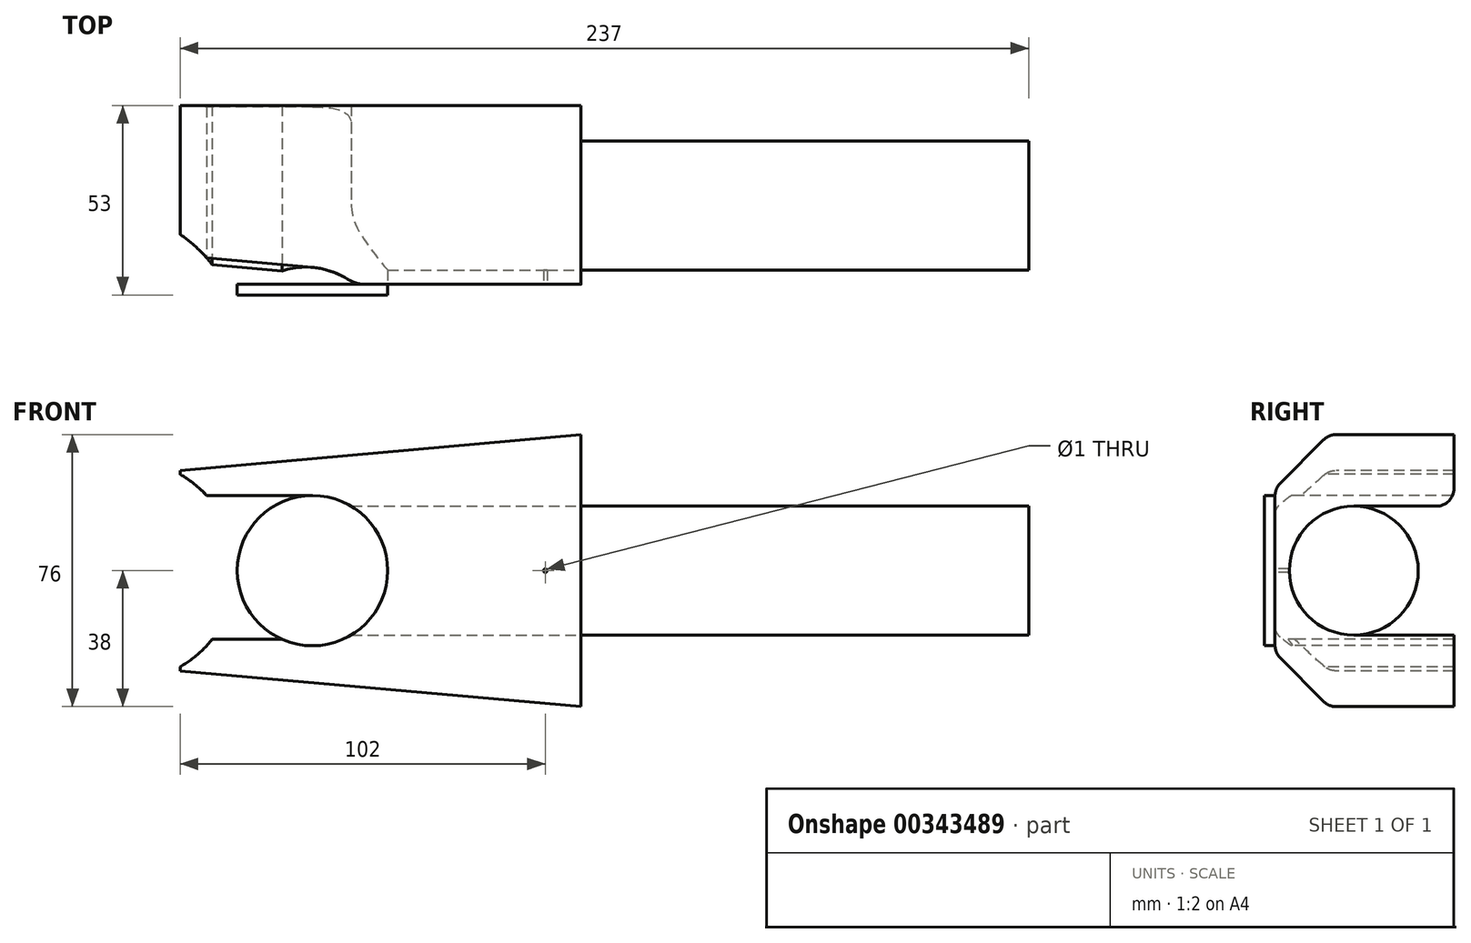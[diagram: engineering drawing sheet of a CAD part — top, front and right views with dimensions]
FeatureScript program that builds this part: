
annotation { "Feature Type Name" : "Feature", "Feature Type Description" : "" }
export const myFeature = defineFeature(function(context is Context, id is Id, definition is map)
    precondition{}
    {
        {
            var Q0;
            Q0=qCreatedBy(makeId("Front.planeOp"),FACE);
            var sketch = newSketch(context, id + "F0", { "sketchPlane" : qUnion([Q0])});
            skCircle(sketch, "E0", {"center": v(0, 0) * mm, "radius": 21 * mm});
            skLineSegment(sketch, "E1", {"start": v(-83.93, 0) * mm, "end": v(59.81, 0) * mm});
            skCircle(sketch, "E2", {"center": v(-52.37, 0) * mm, "radius": 30 * mm});
            skSolve(sketch);
        }
        {
            var Q0;
            Q0=qSketchRegion(id+"F0",true);
            extrude(context, id + "F1", {"entities" : qUnion([Q0]), "endBound" : BoundingType.SYMMETRIC, "depth" : 50 * mm});
        }
        {
            var Q0;
            Q0=qCreatedBy(makeId("Right.planeOp"),FACE);
            var sketch = newSketch(context, id + "F2", { "sketchPlane" : qUnion([Q0])});
            skCircle(sketch, "E3", {"center": v(0, 0) * mm, "radius": 18 * mm});
            skSolve(sketch);
        }
        {
            var Q0;
            Q0=qSketchRegion(id+"F2",true);
            extrude(context, id + "F3", {"entities" : qUnion([Q0]), "operationType" : NewBodyOperationType.ADD, "depth" : 200 * mm});
        }
        {
            var Q0;
            Q0=qCreatedBy(makeId("Front.planeOp"),FACE);
            cPlane(context, id + "F4", {"entities" : qUnion([Q0]), "cplaneType" : CPlaneType.OFFSET, "offset" : 18 * mm, "width" : 150 * mm, "height" : 150 * mm});
        }
        {
            var Q0;
            Q0=qCreatedBy(id+"F4.planeOp",FACE);
            var sketch = newSketch(context, id + "F5", { "sketchPlane" : qUnion([Q0])});
            skCircle(sketch, "E4", {"center": v(65, 0) * mm, "radius": 2.5 * mm});
            skSolve(sketch);
        }
        {
            var Q0;
            Q0=qSketchRegion(id+"F5",true);
            extrude(context, id + "F6", {"entities" : qUnion([Q0]), "operationType" : NewBodyOperationType.REMOVE, "oppositeDirection" : true, "depth" : 30 * mm});
        }
        {
            var Q0;
            Q0=qCreatedBy(makeId("Right.planeOp"),FACE);
            cPlane(context, id + "F7", {"entities" : qUnion([Q0]), "cplaneType" : CPlaneType.OFFSET, "offset" : 10 * mm, "oppositeDirection" : true, "width" : 150 * mm, "height" : 150 * mm});
        }
        {
            var Q0;
            Q0=qCreatedBy(id+"F7.planeOp",FACE);
            var sketch = newSketch(context, id + "F8", { "sketchPlane" : qUnion([Q0])});
            skLineSegment(sketch, "E5", {"start": v(0, 48.61) * mm, "end": v(0, -58.43) * mm});
            skLineSegment(sketch, "E6", {"start": v(-60.37, 0) * mm, "end": v(50.93, 0) * mm});
            skLineSegment(sketch, "E7", {"start": v(0, 24) * mm, "end": v(-10, 24) * mm});
            skLineSegment(sketch, "E8", {"start": v(-10, 24) * mm, "end": v(-10, 28) * mm});
            skLineSegment(sketch, "E9", {"start": v(-10, 28) * mm, "end": v(-1, 28) * mm});
            skLineSegment(sketch, "E10", {"start": v(-1, 28) * mm, "end": v(-1, 29) * mm});
            skLineSegment(sketch, "E11", {"start": v(-1, 29) * mm, "end": v(0, 29) * mm});
            skLineSegment(sketch, "E12.MirrorCS", {"start": v(10, 28) * mm, "end": v(1, 28) * mm});
            skLineSegment(sketch, "E13.MirrorCS", {"start": v(10, 24) * mm, "end": v(10, 28) * mm});
            skLineSegment(sketch, "E14.MirrorCS", {"start": v(0, 24) * mm, "end": v(10, 24) * mm});
            skLineSegment(sketch, "E15.MirrorCS", {"start": v(1, 29) * mm, "end": v(0, 29) * mm});
            skLineSegment(sketch, "E16.MirrorCS", {"start": v(1, 28) * mm, "end": v(1, 29) * mm});
            skLineSegment(sketch, "E17.MirrorCS", {"start": v(1, -28) * mm, "end": v(1, -29) * mm});
            skLineSegment(sketch, "E18.MirrorCS", {"start": v(1, -29) * mm, "end": v(0, -29) * mm});
            skLineSegment(sketch, "E19.MirrorCS", {"start": v(-1, -28) * mm, "end": v(-1, -29) * mm});
            skLineSegment(sketch, "E20.MirrorCS", {"start": v(-1, -29) * mm, "end": v(0, -29) * mm});
            skLineSegment(sketch, "E21.MirrorCS", {"start": v(10, -24) * mm, "end": v(10, -28) * mm});
            skLineSegment(sketch, "E22.MirrorCS", {"start": v(0, -24) * mm, "end": v(10, -24) * mm});
            skLineSegment(sketch, "E23.MirrorCS", {"start": v(0, -24) * mm, "end": v(-10, -24) * mm});
            skLineSegment(sketch, "E24.MirrorCS", {"start": v(-10, -24) * mm, "end": v(-10, -28) * mm});
            skLineSegment(sketch, "E25.MirrorCS", {"start": v(-10, -28) * mm, "end": v(-1, -28) * mm});
            skLineSegment(sketch, "E26.MirrorCS", {"start": v(10, -28) * mm, "end": v(1, -28) * mm});
            skSolve(sketch);
        }
        {
            var Q0;
            {var subQ0=sQuery(id+"F8.wireOp",EDGE,"E7");Q0=makeQuery(id+"F8.imprint","IMPRINT",FACE,{"disambiguationData":[TD([[makeQuery(id+"F8.imprint","IMPRINT",EDGE,{"derivedFrom":subQ0}),-1.0]])]});}
            var Q1;
            Q1=makeQuery(id+"F8.imprint","IMPRINT",FACE,{"disambiguationData":[TD([[makeQuery(id+"F8.imprint","IMPRINT",EDGE,{"derivedFrom":sQuery(id+"F8.wireOp",EDGE,"E12.MirrorCS")}),1.0]])]});
            var Q2;
            Q2=makeQuery(id+"F8.imprint","IMPRINT",FACE,{"disambiguationData":[TD([[makeQuery(id+"F8.imprint","IMPRINT",EDGE,{"derivedFrom":sQuery(id+"F8.wireOp",EDGE,"E19.MirrorCS")}),1.0]])]});
            var Q3;
            Q3=makeQuery(id+"F8.imprint","IMPRINT",FACE,{"disambiguationData":[TD([[makeQuery(id+"F8.imprint","IMPRINT",EDGE,{"derivedFrom":sQuery(id+"F8.wireOp",EDGE,"E17.MirrorCS")}),-1.0]])]});
            extrude(context, id + "F9", {"entities" : qUnion([Q0, Q1, Q2, Q3]), "depth" : 85 * mm});
        }
        {
            var Q0;
            Q0=makeQuery(id+"F9.opExtrude","CAP_FACE",FACE,{"disambiguationData":[OSD([sQuery(id+"F8.wireOp",EDGE,"E7"),sQuery(id+"F8.wireOp",EDGE,"E8"),sQuery(id+"F8.wireOp",EDGE,"E9"),sQuery(id+"F8.wireOp",EDGE,"E10"),sQuery(id+"F8.wireOp",EDGE,"E11"),sQuery(id+"F8.wireOp",EDGE,"E12.MirrorCS"),sQuery(id+"F8.wireOp",EDGE,"E13.MirrorCS"),sQuery(id+"F8.wireOp",EDGE,"E14.MirrorCS"),sQuery(id+"F8.wireOp",EDGE,"E15.MirrorCS"),sQuery(id+"F8.wireOp",EDGE,"E16.MirrorCS")])],"isStart":false});
            var sketch = newSketch(context, id + "F10", { "sketchPlane" : qUnion([Q0])});
            skLineSegment(sketch, "E27", {"start": v(-18, 0) * mm, "end": v(-18, 15.79) * mm});
            skLineSegment(sketch, "E28", {"start": v(-18, 15.79) * mm, "end": v(-10, 24) * mm});
            skLineSegment(sketch, "E29", {"start": v(-56.87, 0) * mm, "end": v(48.34, 0) * mm});
            skLineSegment(sketch, "E30", {"start": v(-10, 28) * mm, "end": v(-20, 17.73) * mm});
            skLineSegment(sketch, "E31", {"start": v(-20, 17.73) * mm, "end": v(-20, 0) * mm});
            skLineSegment(sketch, "E32.MirrorCS", {"start": v(-20, -17.73) * mm, "end": v(-20, 0) * mm});
            skLineSegment(sketch, "E33.MirrorCS", {"start": v(-10, -28) * mm, "end": v(-20, -17.73) * mm});
            skLineSegment(sketch, "E34.MirrorCS", {"start": v(-18, -15.79) * mm, "end": v(-10, -24) * mm});
            skLineSegment(sketch, "E35.MirrorCS", {"start": v(-18, 0) * mm, "end": v(-18, -15.79) * mm});
            skLineSegment(sketch, "E36", {"start": v(-10, -28) * mm, "end": v(-10, -24) * mm});
            skSolve(sketch);
        }
        {
            var Q0;
            {var subQ0=sQuery(id+"F10.wireOp",EDGE,"E32.MirrorCS");Q0=makeQuery(id+"F10.imprint","IMPRINT",FACE,{"disambiguationData":[TD([[makeQuery(id+"F10.imprint","IMPRINT",EDGE,{"derivedFrom":subQ0}),-1.0]])]});}
            var Q1;
            {var subQ1=sQuery(id+"F10.wireOp",EDGE,"E27");Q1=makeQuery(id+"F10.imprint","IMPRINT",FACE,{"disambiguationData":[TD([[makeQuery(id+"F10.imprint","IMPRINT",EDGE,{"derivedFrom":subQ1}),1.0]])]});}
            extrude(context, id + "F11", {"entities" : qUnion([Q0, Q1]), "oppositeDirection" : true, "depth" : 85 * mm});
        }
        {
            var Q0;
            Q0=makeQuery(id+"F11.opExtrude","SWEPT_FACE",FACE,{"disambiguationData":[OSD([sQuery(id+"F10.wireOp",EDGE,"E31"),sQuery(id+"F10.wireOp",EDGE,"E32.MirrorCS")])]});
            var sketch = newSketch(context, id + "F12", { "sketchPlane" : qUnion([Q0])});
            skCircle(sketch, "E37", {"center": v(0, 0) * mm, "radius": 21 * mm});
            skLineSegment(sketch, "E38", {"start": v(0, 21) * mm, "end": v(-10, 21) * mm});
            skLineSegment(sketch, "E39", {"start": v(-10, 21) * mm, "end": v(-10, 18.47) * mm});
            skLineSegment(sketch, "E40", {"start": v(0, -21) * mm, "end": v(-10, -21) * mm});
            skLineSegment(sketch, "E41", {"start": v(-10, -21) * mm, "end": v(-10, -18.47) * mm});
            skSolve(sketch);
        }
        {
            var Q0;
            Q0=qSketchRegion(id+"F12",true);
            extrude(context, id + "F13", {"entities" : qUnion([Q0]), "operationType" : NewBodyOperationType.REMOVE, "endBound" : BoundingType.THROUGH_ALL, "oppositeDirection" : true, "depth" : 30 * mm});
        }
        {
            var Q0;
            Q0=makeQuery(id+"F11.opExtrude","SWEPT_FACE",FACE,{"disambiguationData":[OSD([sQuery(id+"F10.wireOp",EDGE,"E31"),sQuery(id+"F10.wireOp",EDGE,"E32.MirrorCS")])]});
            var sketch = newSketch(context, id + "F14", { "sketchPlane" : qUnion([Q0])});
            skCircle(sketch, "E42", {"center": v(65, 0) * mm, "radius": 2.5 * mm});
            skSolve(sketch);
        }
        {
            var Q0;
            Q0=makeQuery(id+"F14.imprint","IMPRINT",FACE,{"disambiguationData":[TD([[makeQuery(id+"F14.imprint","IMPRINT",EDGE,{"derivedFrom":sQuery(id+"F14.wireOp",EDGE,"E42")}),1.0]])]});
            extrude(context, id + "F15", {"entities" : qUnion([Q0]), "operationType" : NewBodyOperationType.REMOVE, "endBound" : BoundingType.THROUGH_ALL, "oppositeDirection" : true, "depth" : 25 * mm});
        }
        {
            var Q0;
            Q0=makeQuery(id+"F9.opExtrude","SWEPT_BODY",BODY,{"disambiguationData":[OSD([sQuery(id+"F8.wireOp",EDGE,"E7"),sQuery(id+"F8.wireOp",EDGE,"E8"),sQuery(id+"F8.wireOp",EDGE,"E9"),sQuery(id+"F8.wireOp",EDGE,"E10"),sQuery(id+"F8.wireOp",EDGE,"E11"),sQuery(id+"F8.wireOp",EDGE,"E12.MirrorCS"),sQuery(id+"F8.wireOp",EDGE,"E13.MirrorCS"),sQuery(id+"F8.wireOp",EDGE,"E14.MirrorCS"),sQuery(id+"F8.wireOp",EDGE,"E15.MirrorCS"),sQuery(id+"F8.wireOp",EDGE,"E16.MirrorCS")])]});
            var Q1;
            Q1=makeQuery(id+"F9.opExtrude","SWEPT_BODY",BODY,{"disambiguationData":[OSD([sQuery(id+"F8.wireOp",EDGE,"E17.MirrorCS"),sQuery(id+"F8.wireOp",EDGE,"E18.MirrorCS"),sQuery(id+"F8.wireOp",EDGE,"E19.MirrorCS"),sQuery(id+"F8.wireOp",EDGE,"E20.MirrorCS"),sQuery(id+"F8.wireOp",EDGE,"E21.MirrorCS"),sQuery(id+"F8.wireOp",EDGE,"E22.MirrorCS"),sQuery(id+"F8.wireOp",EDGE,"E23.MirrorCS"),sQuery(id+"F8.wireOp",EDGE,"E24.MirrorCS"),sQuery(id+"F8.wireOp",EDGE,"E25.MirrorCS"),sQuery(id+"F8.wireOp",EDGE,"E26.MirrorCS")])]});
            var Q2;
            Q2=makeQuery(id+"F11.opExtrude","SWEPT_BODY",BODY,{"disambiguationData":[OSD([sQuery(id+"F8.wireOp",EDGE,"E8"),sQuery(id+"F10.wireOp",EDGE,"E27"),sQuery(id+"F10.wireOp",EDGE,"E28"),sQuery(id+"F10.wireOp",EDGE,"E30"),sQuery(id+"F10.wireOp",EDGE,"E31"),sQuery(id+"F10.wireOp",EDGE,"E32.MirrorCS"),sQuery(id+"F10.wireOp",EDGE,"E33.MirrorCS"),sQuery(id+"F10.wireOp",EDGE,"E34.MirrorCS"),sQuery(id+"F10.wireOp",EDGE,"E35.MirrorCS"),sQuery(id+"F10.wireOp",EDGE,"E36")])]});
            booleanBodies(context, id + "F16", {"operationType" : BooleanOperationType.UNION, "tools" : qUnion([Q0, Q1, Q2])});
        }
        {
            var Q0;
            {var subQ0=sQuery(id+"F8.wireOp",EDGE,"E9");var subQ1=sQuery(id+"F8.wireOp",EDGE,"E8");Q0=makeQuery(id+"F16.opBoolean","MERGE",EDGE,{"derivedFrom":[makeQuery(id+"F9.opExtrude","SWEPT_EDGE",EDGE,{"disambiguationData":[OSD([subQ1,subQ0])]}),makeQuery(id+"F11.opExtrude","SWEPT_EDGE",EDGE,{"disambiguationData":[OSD([subQ1,subQ0,sQuery(id+"F10.wireOp",EDGE,"E30")])]})]});}
            var Q1;
            Q1=makeQuery(id+"F11.opExtrude","SWEPT_EDGE",EDGE,{"disambiguationData":[OSD([sQuery(id+"F10.wireOp",EDGE,"E30"),sQuery(id+"F10.wireOp",EDGE,"E31")])]});
            var Q2;
            Q2=makeQuery(id+"F11.opExtrude","SWEPT_EDGE",EDGE,{"disambiguationData":[OSD([sQuery(id+"F10.wireOp",EDGE,"E32.MirrorCS"),sQuery(id+"F10.wireOp",EDGE,"E33.MirrorCS")])]});
            var Q3;
            Q3=makeQuery(id+"F16.opBoolean","MERGE",EDGE,{"derivedFrom":[makeQuery(id+"F9.opExtrude","SWEPT_EDGE",EDGE,{"disambiguationData":[OSD([sQuery(id+"F8.wireOp",EDGE,"E24.MirrorCS"),sQuery(id+"F8.wireOp",EDGE,"E25.MirrorCS")])]}),makeQuery(id+"F11.opExtrude","SWEPT_EDGE",EDGE,{"disambiguationData":[OSD([sQuery(id+"F10.wireOp",EDGE,"E33.MirrorCS"),sQuery(id+"F10.wireOp",EDGE,"E36")])]})]});
            fillet(context, id + "F17", {"entities" : qUnion([Q0, Q1, Q2, Q3]), "radius" : 2 * mm, "tangentPropagation" : true, "allowEdgeOverflow" : false});
        }
        {
            var Q0;
            Q0=makeQuery(id+"F9.opExtrude","SWEPT_BODY",BODY,{"disambiguationData":[OSD([sQuery(id+"F8.wireOp",EDGE,"E7"),sQuery(id+"F8.wireOp",EDGE,"E8"),sQuery(id+"F8.wireOp",EDGE,"E9"),sQuery(id+"F8.wireOp",EDGE,"E10"),sQuery(id+"F8.wireOp",EDGE,"E11"),sQuery(id+"F8.wireOp",EDGE,"E12.MirrorCS"),sQuery(id+"F8.wireOp",EDGE,"E13.MirrorCS"),sQuery(id+"F8.wireOp",EDGE,"E14.MirrorCS"),sQuery(id+"F8.wireOp",EDGE,"E15.MirrorCS"),sQuery(id+"F8.wireOp",EDGE,"E16.MirrorCS")])]});
            deleteBodies(context, id + "F18", {"entities" : qUnion([Q0])});
        }
        {
            var Q0;
            Q0=qCreatedBy(id+"F4.planeOp",FACE);
            var sketch = newSketch(context, id + "F19", { "sketchPlane" : qUnion([Q0])});
            skLineSegment(sketch, "E43", {"start": v(75, 0) * mm, "end": v(75, 38) * mm});
            skLineSegment(sketch, "E44", {"start": v(75, 38) * mm, "end": v(-37, 28) * mm});
            skLineSegment(sketch, "E45", {"start": v(-37, 28) * mm, "end": v(-37, 0) * mm});
            skLineSegment(sketch, "E46", {"start": v(-42.03, 0) * mm, "end": v(89.63, 0) * mm});
            skLineSegment(sketch, "E47.MirrorCS", {"start": v(-37, -28) * mm, "end": v(-37, 0) * mm});
            skLineSegment(sketch, "E48.MirrorCS", {"start": v(75, -38) * mm, "end": v(-37, -28) * mm});
            skLineSegment(sketch, "E49.MirrorCS", {"start": v(75, 0) * mm, "end": v(75, -38) * mm});
            skSolve(sketch);
        }
        {
            var Q0;
            {var subQ0=sQuery(id+"F19.wireOp",EDGE,"E43");Q0=makeQuery(id+"F19.imprint","IMPRINT",FACE,{"disambiguationData":[TD([[makeQuery(id+"F19.imprint","IMPRINT",EDGE,{"derivedFrom":subQ0}),1.0]])]});}
            var Q1;
            {var subQ2=sQuery(id+"F19.wireOp",EDGE,"E47.MirrorCS");Q1=makeQuery(id+"F19.imprint","IMPRINT",FACE,{"disambiguationData":[TD([[makeQuery(id+"F19.imprint","IMPRINT",EDGE,{"derivedFrom":subQ2}),-1.0]])]});}
            extrude(context, id + "F20", {"entities" : qUnion([Q0, Q1]), "oppositeDirection" : true, "depth" : 46 * mm});
        }
        {
            var Q0;
            Q0 = qSketchRegion(id + "F19", true);
            extrude(context, id + "F21", {"entities" : qUnion([Q0]), "operationType" : NewBodyOperationType.ADD, "depth" : 4 * mm});
        }
        {
            var Q0;
            Q0=makeQuery(id+"F20.opExtrude","SWEPT_FACE",FACE,{"disambiguationData":[OSD([sQuery(id+"F19.wireOp",EDGE,"E43"),sQuery(id+"F19.wireOp",EDGE,"E49.MirrorCS")])]});
            var sketch = newSketch(context, id + "F22", { "sketchPlane" : qUnion([Q0])});
            skArc(sketch, "E50", {"start": v(0, -18) * mm, "mid": v(-18, 0) * mm, "end": v(0, 18) * mm});
            skLineSegment(sketch, "E51", {"start": v(0, 18) * mm, "end": v(28, 18) * mm});
            skLineSegment(sketch, "E52", {"start": v(0, -18) * mm, "end": v(28, -18) * mm});
            skLineSegment(sketch, "E53", {"start": v(28, -18) * mm, "end": v(28, 18) * mm});
            skSolve(sketch);
        }
        {
            var Q0;
            Q0 = qSketchRegion(id + "F22", true);
            extrude(context, id + "F23", {"entities" : qUnion([Q0]), "operationType" : NewBodyOperationType.REMOVE, "endBound" : BoundingType.THROUGH_ALL, "oppositeDirection" : true, "depth" : 25 * mm});
        }
        {
            var Q0;
            Q0=makeQuery(id+"F21.opExtrude","CAP_FACE",FACE,{"disambiguationData":[OSD([sQuery(id+"F19.wireOp",EDGE,"E43"),sQuery(id+"F19.wireOp",EDGE,"E44"),sQuery(id+"F19.wireOp",EDGE,"E45"),sQuery(id+"F19.wireOp",EDGE,"E47.MirrorCS"),sQuery(id+"F19.wireOp",EDGE,"E48.MirrorCS"),sQuery(id+"F19.wireOp",EDGE,"E49.MirrorCS")])],"isStart":false});
            var sketch = newSketch(context, id + "F24", { "sketchPlane" : qUnion([Q0])});
            skArc(sketch, "E54", {"start": v(0, 21) * mm, "mid": v(20.54, -4.36) * mm, "end": v(-8.52, -19.2) * mm});
            skLineSegment(sketch, "E55", {"start": v(0, 21) * mm, "end": v(-37, 21) * mm});
            skLineSegment(sketch, "E56", {"start": v(-8.52, -19.2) * mm, "end": v(-37, -19.2) * mm});
            skLineSegment(sketch, "E57", {"start": v(-37, -19.2) * mm, "end": v(-37, 21) * mm});
            skSolve(sketch);
        }
        {
            var Q0;
            Q0 = qSketchRegion(id + "F24", true);
            extrude(context, id + "F25", {"entities" : qUnion([Q0]), "operationType" : NewBodyOperationType.REMOVE, "endBound" : BoundingType.THROUGH_ALL, "oppositeDirection" : true, "depth" : 40 * mm});
        }
        {
            var Q0;
            Q0=makeQuery(id+"F21.opExtrude","CAP_EDGE",EDGE,{"disambiguationData":[OSD([sQuery(id+"F19.wireOp",EDGE,"E44")])],"isStart":false});
            var Q1;
            Q1=makeQuery(id+"F21.opExtrude","CAP_EDGE",EDGE,{"disambiguationData":[OSD([sQuery(id+"F19.wireOp",EDGE,"E48.MirrorCS")])],"isStart":false});
            chamfer(context, id + "F26", {"entities" : qUnion([Q0, Q1]), "width" : 15 * mm, "tangentPropagation" : true});
        }
        {
            var Q0;
            {var subQ0=sQuery(id+"F19.wireOp",EDGE,"E44");Q0=makeQuery(id+"F26.opChamfer","BLEND_EDGE",EDGE,{"blendedFrom":[makeQuery(id+"F21.opExtrude","CAP_EDGE",EDGE,{"disambiguationData":[OSD([subQ0])],"isStart":false}),makeQuery(id+"F21.opExtrude","CAP_FACE",FACE,{"disambiguationData":[OSD([sQuery(id+"F19.wireOp",EDGE,"E43"),subQ0,sQuery(id+"F19.wireOp",EDGE,"E45"),sQuery(id+"F19.wireOp",EDGE,"E47.MirrorCS"),sQuery(id+"F19.wireOp",EDGE,"E48.MirrorCS"),sQuery(id+"F19.wireOp",EDGE,"E49.MirrorCS")])],"isStart":false})],"blendedInto":[makeQuery(id+"F21.opExtrude","CAP_FACE",FACE,{"disambiguationData":[OSD([sQuery(id+"F19.wireOp",EDGE,"E43"),subQ0,sQuery(id+"F19.wireOp",EDGE,"E45"),sQuery(id+"F19.wireOp",EDGE,"E47.MirrorCS"),sQuery(id+"F19.wireOp",EDGE,"E48.MirrorCS"),sQuery(id+"F19.wireOp",EDGE,"E49.MirrorCS")])],"isStart":false})]});}
            var Q1;
            {var subQ0=sQuery(id+"F19.wireOp",EDGE,"E44");Q1=makeQuery(id+"F26.opChamfer","BLEND_EDGE",EDGE,{"blendedFrom":[makeQuery(id+"F21.opExtrude","CAP_EDGE",EDGE,{"disambiguationData":[OSD([subQ0])],"isStart":false}),makeQuery(id+"F21.boolean.opBoolean","MERGE",FACE,{"derivedFrom":[makeQuery(id+"F20.opExtrude","SWEPT_FACE",FACE,{"disambiguationData":[OSD([subQ0])]}),makeQuery(id+"F21.opExtrude","SWEPT_FACE",FACE,{"disambiguationData":[OSD([subQ0])]})]})],"blendedInto":[makeQuery(id+"F21.boolean.opBoolean","MERGE",FACE,{"derivedFrom":[makeQuery(id+"F20.opExtrude","SWEPT_FACE",FACE,{"disambiguationData":[OSD([subQ0])]}),makeQuery(id+"F21.opExtrude","SWEPT_FACE",FACE,{"disambiguationData":[OSD([subQ0])]})]})]});}
            var Q2;
            {var subQ0=sQuery(id+"F19.wireOp",EDGE,"E48.MirrorCS");Q2=makeQuery(id+"F26.opChamfer","BLEND_EDGE",EDGE,{"blendedFrom":[makeQuery(id+"F21.opExtrude","CAP_EDGE",EDGE,{"disambiguationData":[OSD([subQ0])],"isStart":false}),makeQuery(id+"F21.opExtrude","CAP_FACE",FACE,{"disambiguationData":[OSD([sQuery(id+"F19.wireOp",EDGE,"E43"),sQuery(id+"F19.wireOp",EDGE,"E44"),sQuery(id+"F19.wireOp",EDGE,"E45"),sQuery(id+"F19.wireOp",EDGE,"E47.MirrorCS"),subQ0,sQuery(id+"F19.wireOp",EDGE,"E49.MirrorCS")])],"isStart":false})],"blendedInto":[makeQuery(id+"F21.opExtrude","CAP_FACE",FACE,{"disambiguationData":[OSD([sQuery(id+"F19.wireOp",EDGE,"E43"),sQuery(id+"F19.wireOp",EDGE,"E44"),sQuery(id+"F19.wireOp",EDGE,"E45"),sQuery(id+"F19.wireOp",EDGE,"E47.MirrorCS"),subQ0,sQuery(id+"F19.wireOp",EDGE,"E49.MirrorCS")])],"isStart":false})]});}
            var Q3;
            {var subQ0=sQuery(id+"F19.wireOp",EDGE,"E48.MirrorCS");Q3=makeQuery(id+"F26.opChamfer","BLEND_EDGE",EDGE,{"blendedFrom":[makeQuery(id+"F21.opExtrude","CAP_EDGE",EDGE,{"disambiguationData":[OSD([subQ0])],"isStart":false}),makeQuery(id+"F21.boolean.opBoolean","MERGE",FACE,{"derivedFrom":[makeQuery(id+"F20.opExtrude","SWEPT_FACE",FACE,{"disambiguationData":[OSD([subQ0])]}),makeQuery(id+"F21.opExtrude","SWEPT_FACE",FACE,{"disambiguationData":[OSD([subQ0])]})]})],"blendedInto":[makeQuery(id+"F21.boolean.opBoolean","MERGE",FACE,{"derivedFrom":[makeQuery(id+"F20.opExtrude","SWEPT_FACE",FACE,{"disambiguationData":[OSD([subQ0])]}),makeQuery(id+"F21.opExtrude","SWEPT_FACE",FACE,{"disambiguationData":[OSD([subQ0])]})]})]});}
            fillet(context, id + "F27", {"entities" : qUnion([Q0, Q1, Q2, Q3]), "radius" : 5 * mm, "tangentPropagation" : true, "allowEdgeOverflow" : false});
        }
        {
            var Q0;
            Q0=makeQuery(id+"F21.opExtrude","CAP_FACE",FACE,{"disambiguationData":[OSD([sQuery(id+"F19.wireOp",EDGE,"E43"),sQuery(id+"F19.wireOp",EDGE,"E44"),sQuery(id+"F19.wireOp",EDGE,"E45"),sQuery(id+"F19.wireOp",EDGE,"E47.MirrorCS"),sQuery(id+"F19.wireOp",EDGE,"E48.MirrorCS"),sQuery(id+"F19.wireOp",EDGE,"E49.MirrorCS")])],"isStart":false});
            var sketch = newSketch(context, id + "F28", { "sketchPlane" : qUnion([Q0])});
            skCircle(sketch, "E58", {"center": v(65, 0) * mm, "radius": 0.5 * mm});
            skSolve(sketch);
        }
        {
            var Q0;
            Q0=makeQuery(id+"F28.imprint","IMPRINT",FACE,{"disambiguationData":[TD([[makeQuery(id+"F28.imprint","IMPRINT",EDGE,{"derivedFrom":sQuery(id+"F28.wireOp",EDGE,"E58")}),1.0]])]});
            extrude(context, id + "F29", {"entities" : qUnion([Q0]), "operationType" : NewBodyOperationType.REMOVE, "endBound" : BoundingType.UP_TO_NEXT, "oppositeDirection" : true, "depth" : 25 * mm});
        }
        {
            var Q0;
            Q0=makeQuery(id+"F23.boolean.opBoolean","COPY",EDGE,{"derivedFrom":makeQuery(id+"F23.opExtrude","SWEPT_EDGE",EDGE,{"disambiguationData":[OSD([sQuery(id+"F19.wireOp",EDGE,"E43"),sQuery(id+"F19.wireOp",EDGE,"E49.MirrorCS"),sQuery(id+"F22.wireOp",EDGE,"E51"),sQuery(id+"F22.wireOp",EDGE,"E53")])]})});
            var Q1;
            Q1=makeQuery(id+"F23.boolean.opBoolean","COPY",EDGE,{"derivedFrom":makeQuery(id+"F23.opExtrude","SWEPT_EDGE",EDGE,{"disambiguationData":[OSD([sQuery(id+"F19.wireOp",EDGE,"E43"),sQuery(id+"F19.wireOp",EDGE,"E49.MirrorCS"),sQuery(id+"F22.wireOp",EDGE,"E52"),sQuery(id+"F22.wireOp",EDGE,"E53")])]})});
            fillet(context, id + "F30", {"entities" : qUnion([Q0, Q1]), "radius" : 5 * mm, "tangentPropagation" : true, "allowEdgeOverflow" : false});
        }
        {
            var Q0;
            Q0=makeQuery(id+"F1.opExtrude","CAP_FACE",FACE,{"disambiguationData":[OSD([sQuery(id+"F0.wireOp",EDGE,"E2")])],"isStart":false});
            var sketch = newSketch(context, id + "F31", { "sketchPlane" : qUnion([Q0])});
            skCircle(sketch, "E59", {"center": v(-52.37, 0) * mm, "radius": 31 * mm});
            skSolve(sketch);
        }
        {
            var Q0;
            Q0 = qSketchRegion(id + "F31", true);
            extrude(context, id + "F32", {"entities" : qUnion([Q0]), "operationType" : NewBodyOperationType.REMOVE, "endBound" : BoundingType.THROUGH_ALL, "oppositeDirection" : true, "depth" : 25 * mm});
        }
    });
